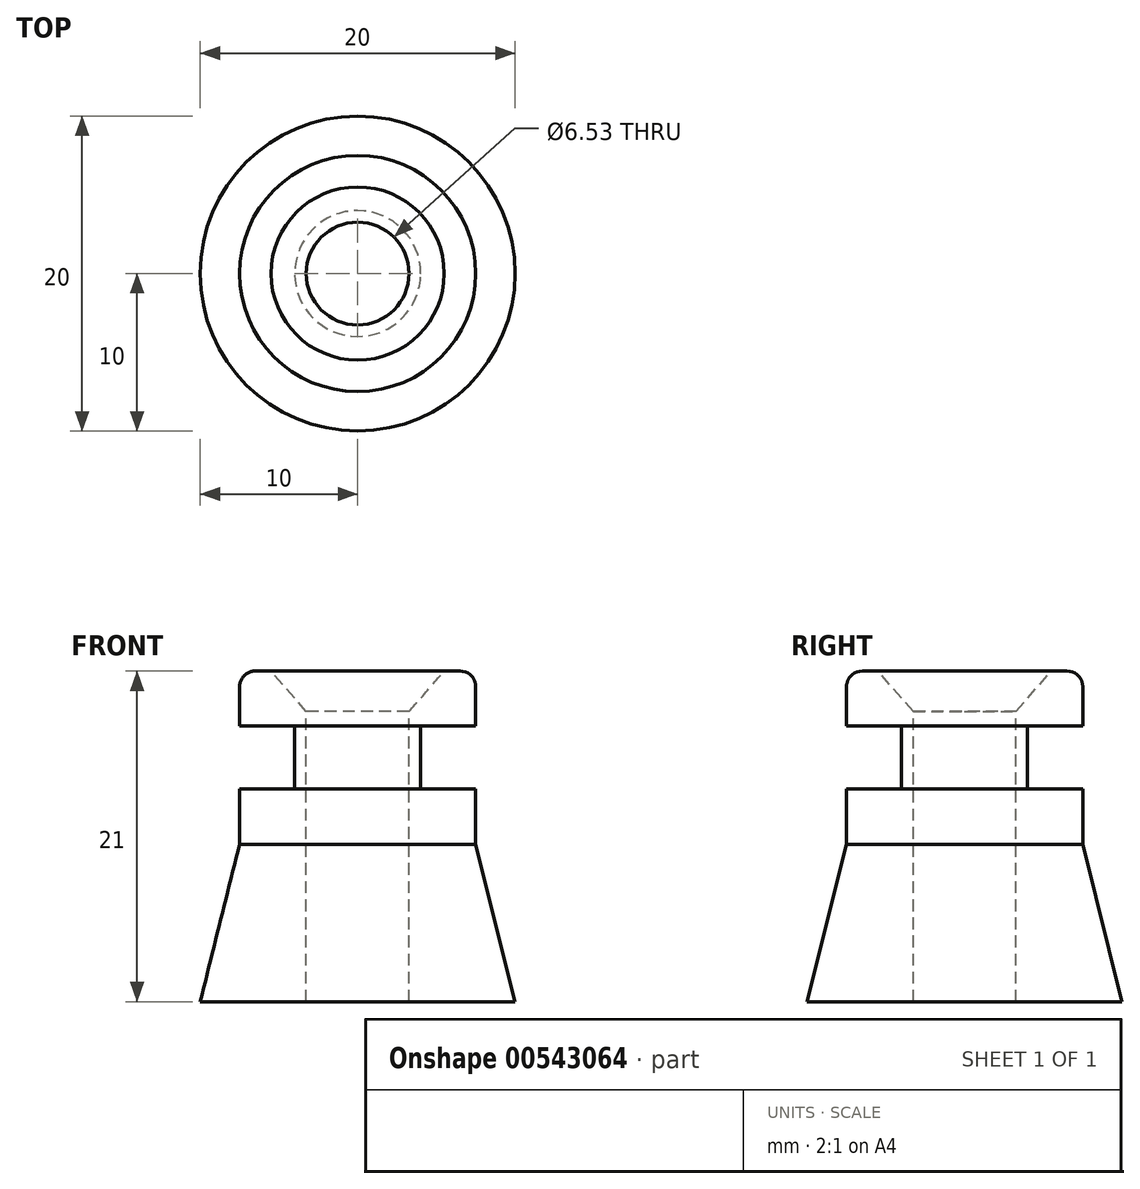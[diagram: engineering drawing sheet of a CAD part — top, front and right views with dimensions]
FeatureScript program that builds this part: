
annotation { "Feature Type Name" : "Feature", "Feature Type Description" : "" }
export const myFeature = defineFeature(function(context is Context, id is Id, definition is map)
    precondition{}
    {
        {
            var Q0;
            Q0=qCreatedBy(makeId("Front.planeOp"),FACE);
            var sketch = newSketch(context, id + "F0", { "sketchPlane" : qUnion([Q0])});
            skLineSegment(sketch, "E0", {"start": v(0, 0) * mm, "end": v(0, 5.5) * mm});
            skLineSegment(sketch, "E1", {"start": v(0, 5.5) * mm, "end": v(7.5, 5.5) * mm});
            skLineSegment(sketch, "E2", {"start": v(7.5, 5.5) * mm, "end": v(7.5, 2) * mm});
            skLineSegment(sketch, "E3", {"start": v(7.5, 2) * mm, "end": v(4, 2) * mm});
            skLineSegment(sketch, "E4", {"start": v(4, 2) * mm, "end": v(4, 0) * mm});
            skLineSegment(sketch, "E5.MirrorCS", {"start": v(0, 0) * mm, "end": v(0, -5.5) * mm});
            skLineSegment(sketch, "E6.MirrorCS", {"start": v(0, -5.5) * mm, "end": v(7.5, -5.5) * mm});
            skLineSegment(sketch, "E7.MirrorCS", {"start": v(7.5, -5.5) * mm, "end": v(7.5, -2) * mm});
            skLineSegment(sketch, "E8.MirrorCS", {"start": v(7.5, -2) * mm, "end": v(4, -2) * mm});
            skLineSegment(sketch, "E9.MirrorCS", {"start": v(4, -2) * mm, "end": v(4, 0) * mm});
            skSolve(sketch);
        }
        {
            var Q0;
            Q0=makeQuery(id+"F0.imprint","IMPRINT",FACE,{"disambiguationData":[TD([[makeQuery(id+"F0.imprint","IMPRINT",EDGE,{"derivedFrom":sQuery(id+"F0.wireOp",EDGE,"E0")}),-1.0]])]});
            var Q1;
            Q1=sQuery(id+"F0.wireOp",EDGE,"E0");
            revolve(context, id + "F1", {"entities" : qUnion([Q0]), "axis" : qUnion([Q1]), "revolveType" : RevolveType.FULL});
        }
        {
            var Q0;
            Q0=makeQuery(id+"F1.opRevolve","SWEPT_FACE",FACE,{"disambiguationData":[OSD([sQuery(id+"F0.wireOp",EDGE,"E6.MirrorCS")])]});
            cPlane(context, id + "F2", {"entities" : qUnion([Q0]), "cplaneType" : CPlaneType.OFFSET, "offset" : 10 * mm, "width" : 152.4 * mm, "height" : 152.4 * mm});
        }
        {
            var Q0;
            Q0=qCreatedBy(id+"F2.planeOp",FACE);
            var sketch = newSketch(context, id + "F3", { "sketchPlane" : qUnion([Q0])});
            skCircle(sketch, "E10", {"center": v(0, 0) * mm, "radius": 10 * mm});
            skSolve(sketch);
        }
        {
            var Q1;
            Q1=makeQuery(id+"F1.opRevolve","SWEPT_FACE",FACE,{"disambiguationData":[OSD([sQuery(id+"F0.wireOp",EDGE,"E6.MirrorCS")])]});
            var Q2;
            Q2=makeQuery(id+"F3.imprint","IMPRINT",FACE,{"disambiguationData":[TD([[makeQuery(id+"F3.imprint","IMPRINT",EDGE,{"derivedFrom":sQuery(id+"F3.wireOp",EDGE,"E10")}),1.0]])]});
            loft(context, id + "F4", {"operationType" : NewBodyOperationType.ADD, "sheetProfilesArray" : [{ "sheetProfileEntities" : qUnion([Q1]) }, { "sheetProfileEntities" : qUnion([Q2]) }]});
        }
        {
            var Q0;
            Q0=makeQuery(id+"F1.opRevolve","SWEPT_FACE",FACE,{"disambiguationData":[OSD([sQuery(id+"F0.wireOp",EDGE,"E1")])]});
            var sketch = newSketch(context, id + "F5", { "sketchPlane" : qUnion([Q0])});
            skCircle(sketch, "E11", {"center": v(0, 0) * mm, "radius": 3.69 * mm});
            skSolve(sketch);
        }
        {
            var Q0;
            Q0=sQuery(id+"F5.wireOp",VERTEX,"E11.center");
            var Q1;
            Q1=makeQuery(id+"F1.opRevolve","SWEPT_BODY",BODY,{"disambiguationData":[OSD([sQuery(id+"F0.wireOp",EDGE,"E0"),sQuery(id+"F0.wireOp",EDGE,"E1"),sQuery(id+"F0.wireOp",EDGE,"E2"),sQuery(id+"F0.wireOp",EDGE,"E3"),sQuery(id+"F0.wireOp",EDGE,"E4"),sQuery(id+"F0.wireOp",EDGE,"E5.MirrorCS"),sQuery(id+"F0.wireOp",EDGE,"E6.MirrorCS"),sQuery(id+"F0.wireOp",EDGE,"E7.MirrorCS"),sQuery(id+"F0.wireOp",EDGE,"E8.MirrorCS"),sQuery(id+"F0.wireOp",EDGE,"E9.MirrorCS")])]});
            hole(context, id + "F6", {"style" : HoleStyle.C_SINK, "endStyle" : HoleEndStyle.THROUGH, "holeDiameter" : 6.53 * mm, "cSinkDiameter" : 11 * mm, "cSinkAngle" : 82 * degree, "isTappedThrough" : true, "tappedDepth" : 12.7 * mm, "tapClearance" : 3, "locations" : qUnion([Q0]), "scope" : qUnion([Q1])});
        }
        {
            var Q0;
            Q0=makeQuery(id+"F1.opRevolve","SWEPT_EDGE",EDGE,{"disambiguationData":[OSD([sQuery(id+"F0.wireOp",EDGE,"E1"),sQuery(id+"F0.wireOp",EDGE,"E2")])]});
            fillet(context, id + "F7", {"entities" : qUnion([Q0]), "radius" : 1 * mm, "tangentPropagation" : true, "allowEdgeOverflow" : false});
        }
    });
